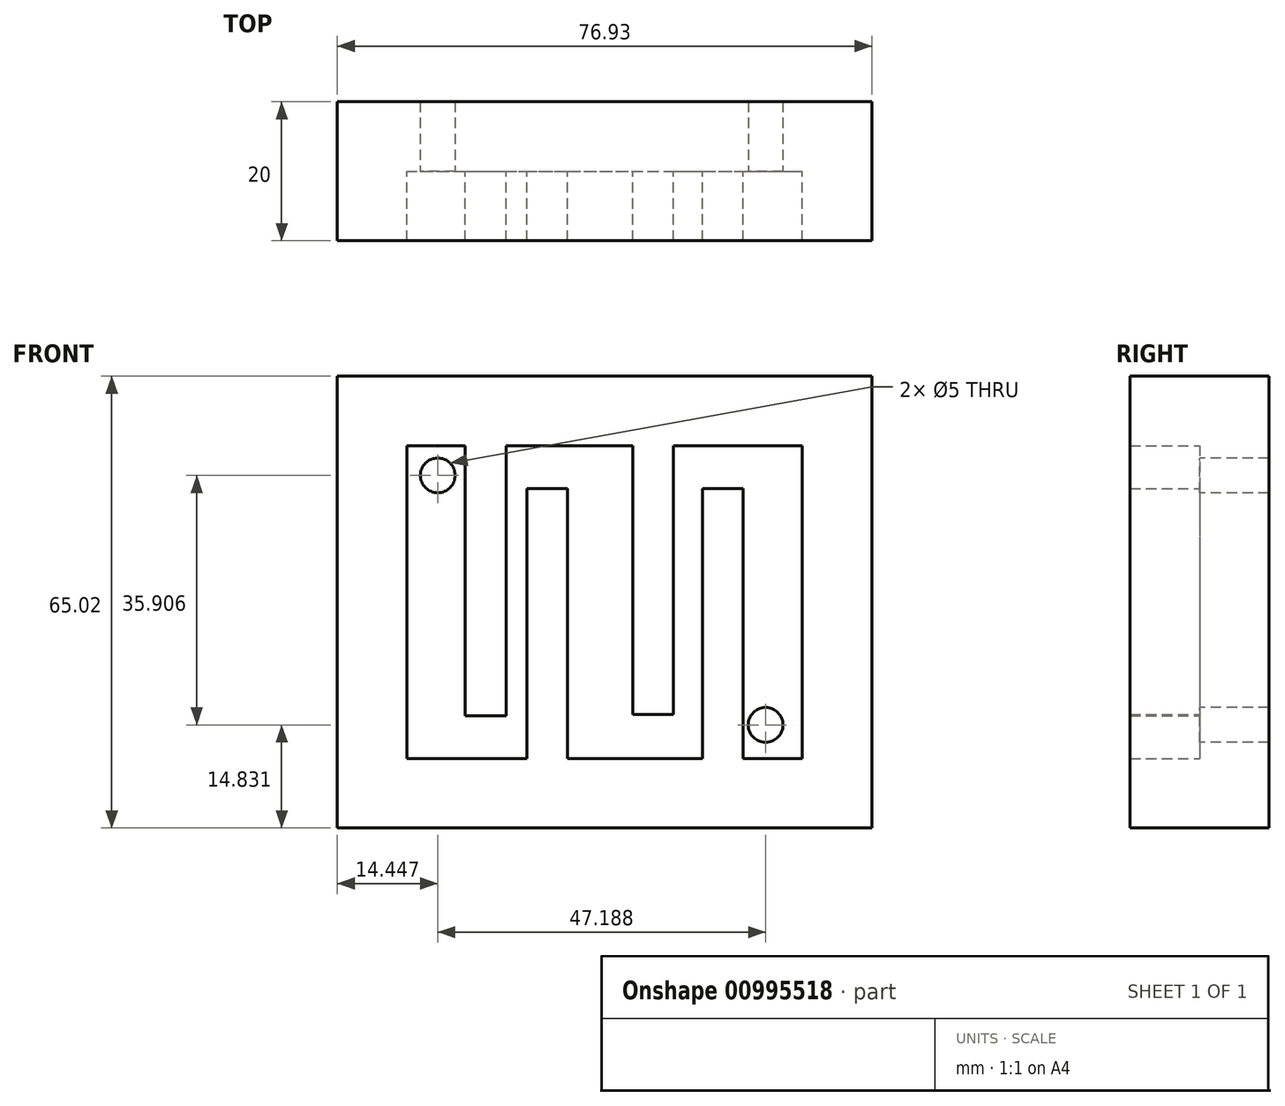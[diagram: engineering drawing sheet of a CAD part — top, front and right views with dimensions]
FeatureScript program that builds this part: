
annotation { "Feature Type Name" : "Feature", "Feature Type Description" : "" }
export const myFeature = defineFeature(function(context is Context, id is Id, definition is map)
    precondition{}
    {
        {
            var Q0;
            Q0=qCreatedBy(makeId("Front.planeOp"),FACE);
            var sketch = newSketch(context, id + "F0", { "sketchPlane" : qUnion([Q0])});
            skLineSegment(sketch, "E0.bottom", {"start": v(-38.5, 33.64) * mm, "end": v(38.43, 33.64) * mm});
            skLineSegment(sketch, "E0.top", {"start": v(-38.5, -31.38) * mm, "end": v(38.43, -31.38) * mm});
            skLineSegment(sketch, "E0.left", {"start": v(-38.5, 33.64) * mm, "end": v(-38.5, -31.38) * mm});
            skLineSegment(sketch, "E0.right", {"start": v(38.43, 33.64) * mm, "end": v(38.43, -31.38) * mm});
            skSolve(sketch);
        }
        {
            var Q0;
            Q0=makeQuery(id+"F0.imprint","IMPRINT",FACE,{"disambiguationData":[TD([[makeQuery(id+"F0.imprint","IMPRINT",EDGE,{"derivedFrom":sQuery(id+"F0.wireOp",EDGE,"E0.bottom")}),-1.0]])]});
            extrude(context, id + "F1", {"entities" : qUnion([Q0]), "depth" : 20 * mm, "offsetDistance" : 25.4 * mm});
        }
        {
            var Q0;
            Q0=makeQuery(id+"F1.opExtrude","CAP_FACE",FACE,{"disambiguationData":[OSD([sQuery(id+"F0.wireOp",EDGE,"E0.bottom"),sQuery(id+"F0.wireOp",EDGE,"E0.top"),sQuery(id+"F0.wireOp",EDGE,"E0.left"),sQuery(id+"F0.wireOp",EDGE,"E0.right")])],"isStart":false});
            shell(context, id + "F2", {"entities" : qUnion([Q0]), "thickness" : 10 * mm});
        }
        {
            var Q0;
            Q0=makeQuery(id+"F2.opShell","OFFSET_FACE",FACE,{"disambiguationData":[OSD([sQuery(id+"F0.wireOp",EDGE,"E0.bottom"),sQuery(id+"F0.wireOp",EDGE,"E0.top"),sQuery(id+"F0.wireOp",EDGE,"E0.left"),sQuery(id+"F0.wireOp",EDGE,"E0.right")])]});
            var sketch = newSketch(context, id + "F3", { "sketchPlane" : qUnion([Q0])});
            skCircle(sketch, "E1", {"center": v(-24.05, 19.36) * mm, "radius": 2.5 * mm});
            skCircle(sketch, "E2", {"center": v(23.14, -16.55) * mm, "radius": 2.5 * mm});
            skSolve(sketch);
        }
        {
            var Q0;
            Q0=sQuery(id+"F3.wireOp",VERTEX,"E1.center");
            var Q1;
            Q1=sQuery(id+"F3.wireOp",VERTEX,"E2.center");
            var Q2;
            Q2=makeQuery(id+"F1.opExtrude","SWEPT_BODY",BODY,{"disambiguationData":[OSD([sQuery(id+"F0.wireOp",EDGE,"E0.bottom"),sQuery(id+"F0.wireOp",EDGE,"E0.top"),sQuery(id+"F0.wireOp",EDGE,"E0.left"),sQuery(id+"F0.wireOp",EDGE,"E0.right")])]});
            hole(context, id + "F4", {"style" : HoleStyle.SIMPLE, "endStyle" : HoleEndStyle.THROUGH, "holeDiameter" : 5 * mm, "majorDiameter" : 5 * mm, "isTappedThrough" : true, "tappedDepth" : 12 * mm, "tapClearance" : 3, "locations" : qUnion([Q0, Q1]), "scope" : qUnion([Q2])});
        }
        {
            var Q0;
            Q0=makeQuery(id+"F2.opShell","OFFSET_FACE",FACE,{"disambiguationData":[OSD([sQuery(id+"F0.wireOp",EDGE,"E0.bottom"),sQuery(id+"F0.wireOp",EDGE,"E0.top"),sQuery(id+"F0.wireOp",EDGE,"E0.left"),sQuery(id+"F0.wireOp",EDGE,"E0.right")])]});
            var sketch = newSketch(context, id + "F5", { "sketchPlane" : qUnion([Q0])});
            skLineSegment(sketch, "E3.bottom", {"start": v(-20.09, 23.64) * mm, "end": v(-14.2, 23.64) * mm});
            skLineSegment(sketch, "E3.top", {"start": v(-20.09, -15.21) * mm, "end": v(-14.2, -15.21) * mm});
            skLineSegment(sketch, "E3.left", {"start": v(-20.09, 23.64) * mm, "end": v(-20.09, -15.21) * mm});
            skLineSegment(sketch, "E3.right", {"start": v(-14.2, 23.64) * mm, "end": v(-14.2, -15.21) * mm});
            skLineSegment(sketch, "E4.bottom", {"start": v(-11.25, 17.47) * mm, "end": v(-5.36, 17.47) * mm});
            skLineSegment(sketch, "E4.top", {"start": v(-11.25, -21.38) * mm, "end": v(-5.36, -21.38) * mm});
            skLineSegment(sketch, "E4.left", {"start": v(-11.25, 17.47) * mm, "end": v(-11.25, -21.38) * mm});
            skLineSegment(sketch, "E4.right", {"start": v(-5.36, 17.47) * mm, "end": v(-5.36, -21.38) * mm});
            skLineSegment(sketch, "E5.bottom", {"start": v(14.03, 17.47) * mm, "end": v(19.92, 17.47) * mm});
            skLineSegment(sketch, "E5.top", {"start": v(14.03, -21.38) * mm, "end": v(19.92, -21.38) * mm});
            skLineSegment(sketch, "E5.left", {"start": v(14.03, 17.47) * mm, "end": v(14.03, -21.38) * mm});
            skLineSegment(sketch, "E5.right", {"start": v(19.92, 17.47) * mm, "end": v(19.92, -21.38) * mm});
            skLineSegment(sketch, "E6.bottom", {"start": v(4, 23.83) * mm, "end": v(9.88, 23.83) * mm});
            skLineSegment(sketch, "E6.top", {"start": v(4, -15.02) * mm, "end": v(9.88, -15.02) * mm});
            skLineSegment(sketch, "E6.left", {"start": v(4, 23.83) * mm, "end": v(4, -15.02) * mm});
            skLineSegment(sketch, "E6.right", {"start": v(9.88, 23.83) * mm, "end": v(9.88, -15.02) * mm});
            skSolve(sketch);
        }
        {
            var Q0;
            Q0 = qSketchRegion(id + "F5", true);
            extrude(context, id + "F6", {"entities" : qUnion([Q0]), "operationType" : NewBodyOperationType.ADD, "depth" : 10 * mm, "offsetDistance" : 25 * mm});
        }
    });
